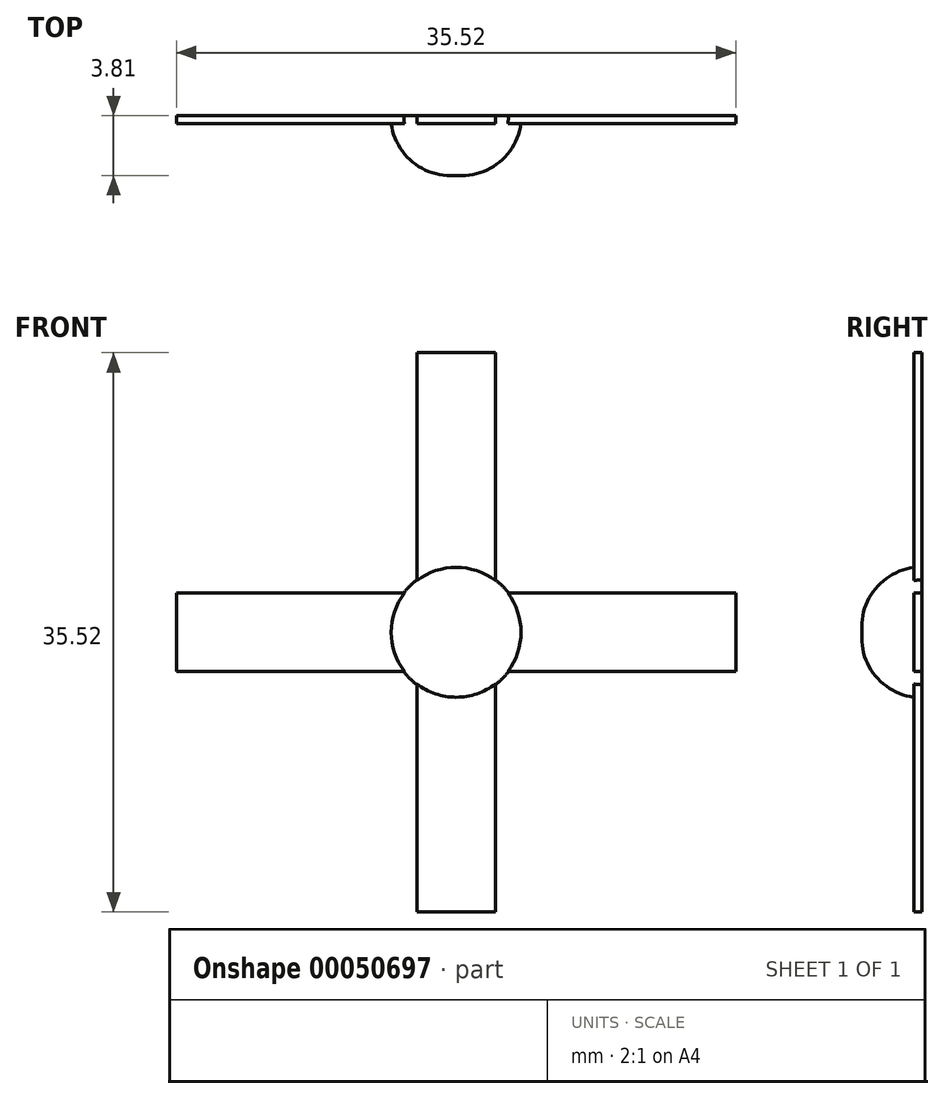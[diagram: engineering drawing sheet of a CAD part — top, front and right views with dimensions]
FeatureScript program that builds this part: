
annotation { "Feature Type Name" : "Feature", "Feature Type Description" : "" }
export const myFeature = defineFeature(function(context is Context, id is Id, definition is map)
    precondition{}
    {
        {
            var Q0;
            Q0=qCreatedBy(makeId("Front.planeOp"),FACE);
            var sketch = newSketch(context, id + "F0", { "sketchPlane" : qUnion([Q0])});
            skCircle(sketch, "E0", {"center": v(0, 0) * mm, "radius": 4.16 * mm});
            skSolve(sketch);
        }
        {
            var Q0;
            Q0=makeQuery(id+"F0.imprint","IMPRINT",FACE,{"disambiguationData":[TD([[makeQuery(id+"F0.imprint","IMPRINT",EDGE,{"derivedFrom":sQuery(id+"F0.wireOp",EDGE,"E0")}),1.0]])]});
            extrude(context, id + "F1", {"entities" : qUnion([Q0]), "depth" : 3.8 * mm});
        }
        {
            var Q0;
            Q0=qCreatedBy(makeId("Front.planeOp"),FACE);
            var sketch = newSketch(context, id + "F2", { "sketchPlane" : qUnion([Q0])});
            skLineSegment(sketch, "E1.rect.bottom", {"start": v(-17.76, 2.5) * mm, "end": v(17.76, 2.5) * mm});
            skLineSegment(sketch, "E1.rect.top", {"start": v(-17.76, -2.5) * mm, "end": v(17.76, -2.5) * mm});
            skLineSegment(sketch, "E1.rect.left", {"start": v(-17.76, 2.5) * mm, "end": v(-17.76, -2.5) * mm});
            skLineSegment(sketch, "E1.rect.right", {"start": v(17.76, 2.5) * mm, "end": v(17.76, -2.5) * mm});
            skPoint(sketch, "E1.rect.middle", {"position": v(0, 0) * mm});
            skLineSegment(sketch, "E2.rect.bottom", {"start": v(-2.5, 17.76) * mm, "end": v(2.5, 17.76) * mm});
            skLineSegment(sketch, "E2.rect.top", {"start": v(-2.5, -17.76) * mm, "end": v(2.5, -17.76) * mm});
            skLineSegment(sketch, "E2.rect.left", {"start": v(-2.5, 17.76) * mm, "end": v(-2.5, -17.76) * mm});
            skLineSegment(sketch, "E2.rect.right", {"start": v(2.5, 17.76) * mm, "end": v(2.5, -17.76) * mm});
            skSolve(sketch);
        }
        {
            var Q0;
            {var subQ5=sQuery(id+"F2.wireOp",EDGE,"E2.rect.bottom");Q0=makeQuery(id+"F2.imprint","IMPRINT",FACE,{"disambiguationData":[TD([[makeQuery(id+"F2.imprint","IMPRINT",EDGE,{"derivedFrom":subQ5}),-1.0]])]});}
            var Q1;
            {var subQ0=sQuery(id+"F2.wireOp",EDGE,"E1.rect.left");Q1=makeQuery(id+"F2.imprint","IMPRINT",FACE,{"disambiguationData":[TD([[makeQuery(id+"F2.imprint","IMPRINT",EDGE,{"derivedFrom":subQ0}),1.0]])]});}
            var Q2;
            {var subQ0=sQuery(id+"F2.wireOp",EDGE,"E2.rect.left");var subQ1=sQuery(id+"F2.wireOp",EDGE,"E1.rect.bottom");var subQ2=makeQuery(id+"F2.imprint","INTERSECT",VERTEX,{"derivedFrom":[subQ1,subQ0]});Q2=makeQuery(id+"F2.imprint","IMPRINT",FACE,{"disambiguationData":[TD([[makeQuery(id+"F2.imprint","IMPRINT",EDGE,{"disambiguationData":[TD([[subQ2,-1.0]])],"derivedFrom":subQ1}),-1.0]])]});}
            var Q3;
            {var subQ5=sQuery(id+"F2.wireOp",EDGE,"E2.rect.top");Q3=makeQuery(id+"F2.imprint","IMPRINT",FACE,{"disambiguationData":[TD([[makeQuery(id+"F2.imprint","IMPRINT",EDGE,{"derivedFrom":subQ5}),1.0]])]});}
            var Q4;
            {var subQ0=sQuery(id+"F2.wireOp",EDGE,"E1.rect.right");Q4=makeQuery(id+"F2.imprint","IMPRINT",FACE,{"disambiguationData":[TD([[makeQuery(id+"F2.imprint","IMPRINT",EDGE,{"derivedFrom":subQ0}),-1.0]])]});}
            extrude(context, id + "F3", {"entities" : qUnion([Q0, Q1, Q2, Q3, Q4]), "operationType" : NewBodyOperationType.ADD, "depth" : 0.5 * mm});
        }
        {
            var Q0;
            Q0=makeQuery(id+"F1.opExtrude","CAP_EDGE",EDGE,{"disambiguationData":[OSD([sQuery(id+"F0.wireOp",EDGE,"E0")])],"isStart":false});
            fillet(context, id + "F4", {"entities" : qUnion([Q0]), "radius" : 3.8 * mm, "tangentPropagation" : true, "allowEdgeOverflow" : false});
        }
    });
